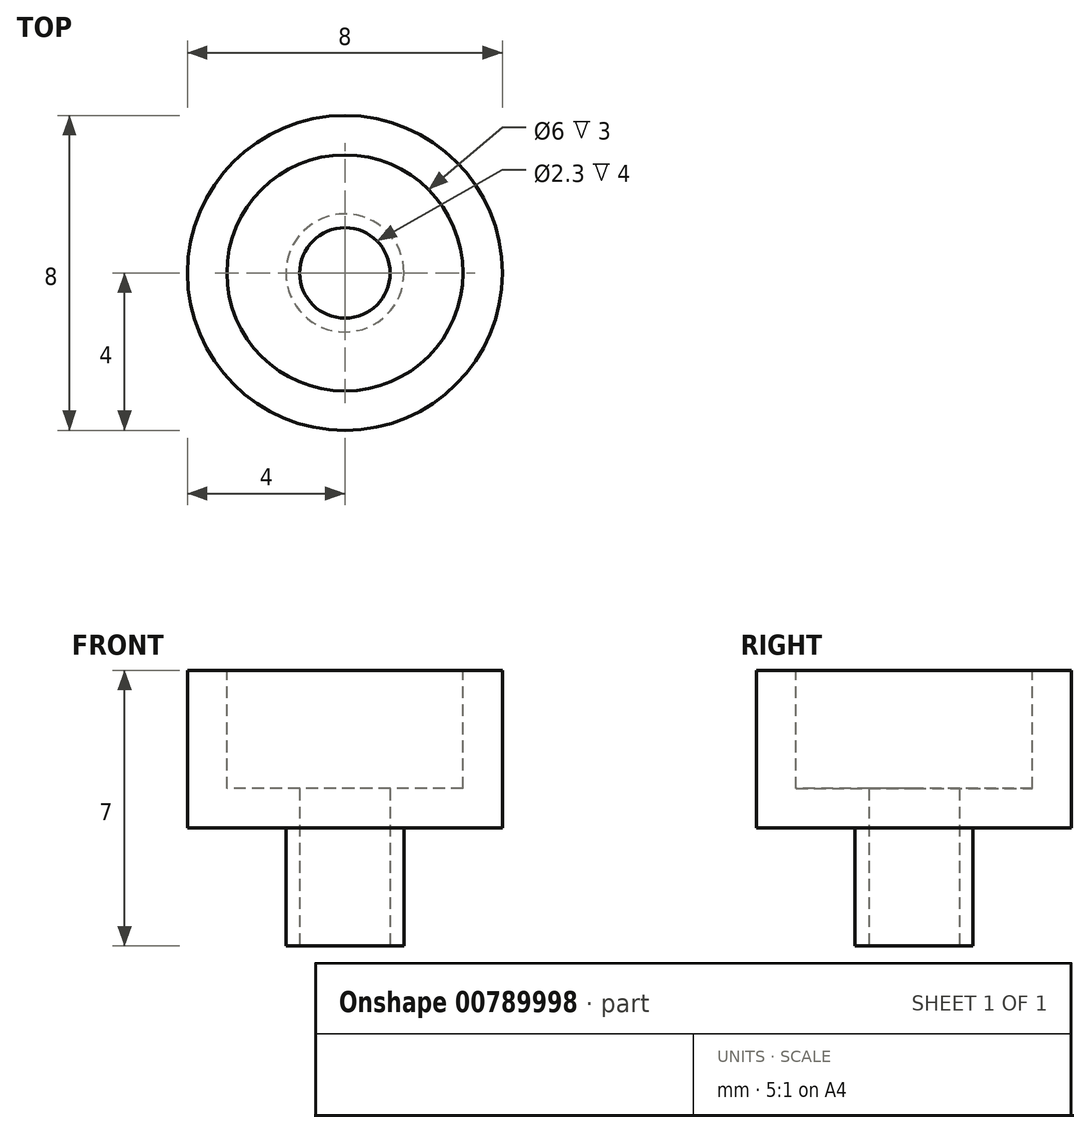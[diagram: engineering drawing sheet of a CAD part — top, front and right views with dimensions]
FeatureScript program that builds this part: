
annotation { "Feature Type Name" : "Feature", "Feature Type Description" : "" }
export const myFeature = defineFeature(function(context is Context, id is Id, definition is map)
    precondition{}
    {
        {
            var Q0;
            Q0=qCreatedBy(makeId("Top.planeOp"),FACE);
            var sketch = newSketch(context, id + "F0", { "sketchPlane" : qUnion([Q0])});
            skCircle(sketch, "E0", {"center": v(0, 0) * mm, "radius": 4 * mm});
            skSolve(sketch);
        }
        {
            var Q0;
            Q0 = qSketchRegion(id + "F0", true);
            extrude(context, id + "F1", {"entities" : qUnion([Q0]), "depth" : 4 * mm, "offsetDistance" : 25 * mm});
        }
        {
            var Q0;
            Q0=makeQuery(id+"F1.opExtrude","CAP_FACE",FACE,{"disambiguationData":[OSD([sQuery(id+"F0.wireOp",EDGE,"E0")])],"isStart":true});
            var sketch = newSketch(context, id + "F2", { "sketchPlane" : qUnion([Q0])});
            skCircle(sketch, "E1", {"center": v(0, 0) * mm, "radius": 1.5 * mm});
            skSolve(sketch);
        }
        {
            var Q0;
            Q0 = qSketchRegion(id + "F2", true);
            extrude(context, id + "F3", {"entities" : qUnion([Q0]), "operationType" : NewBodyOperationType.ADD, "depth" : 3 * mm, "offsetDistance" : 25 * mm});
        }
        {
            var Q0;
            Q0=makeQuery(id+"F1.opExtrude","CAP_FACE",FACE,{"disambiguationData":[OSD([sQuery(id+"F0.wireOp",EDGE,"E0")])],"isStart":false});
            var sketch = newSketch(context, id + "F4", { "sketchPlane" : qUnion([Q0])});
            skCircle(sketch, "E2", {"center": v(0, 0) * mm, "radius": 3 * mm});
            skSolve(sketch);
        }
        {
            var Q0;
            Q0 = qSketchRegion(id + "F4", true);
            extrude(context, id + "F5", {"entities" : qUnion([Q0]), "operationType" : NewBodyOperationType.REMOVE, "oppositeDirection" : true, "depth" : 3 * mm, "offsetDistance" : 25 * mm});
        }
        {
            var Q0;
            Q0=makeQuery(id+"F3.opExtrude","CAP_FACE",FACE,{"disambiguationData":[OSD([sQuery(id+"F2.wireOp",EDGE,"E1")])],"isStart":false});
            var sketch = newSketch(context, id + "F6", { "sketchPlane" : qUnion([Q0])});
            skCircle(sketch, "E3", {"center": v(0, 0) * mm, "radius": 1.15 * mm});
            skSolve(sketch);
        }
        {
            var Q0;
            Q0 = qSketchRegion(id + "F6", true);
            extrude(context, id + "F7", {"entities" : qUnion([Q0]), "operationType" : NewBodyOperationType.REMOVE, "oppositeDirection" : true, "depth" : 25 * mm, "offsetDistance" : 25 * mm});
        }
    });
